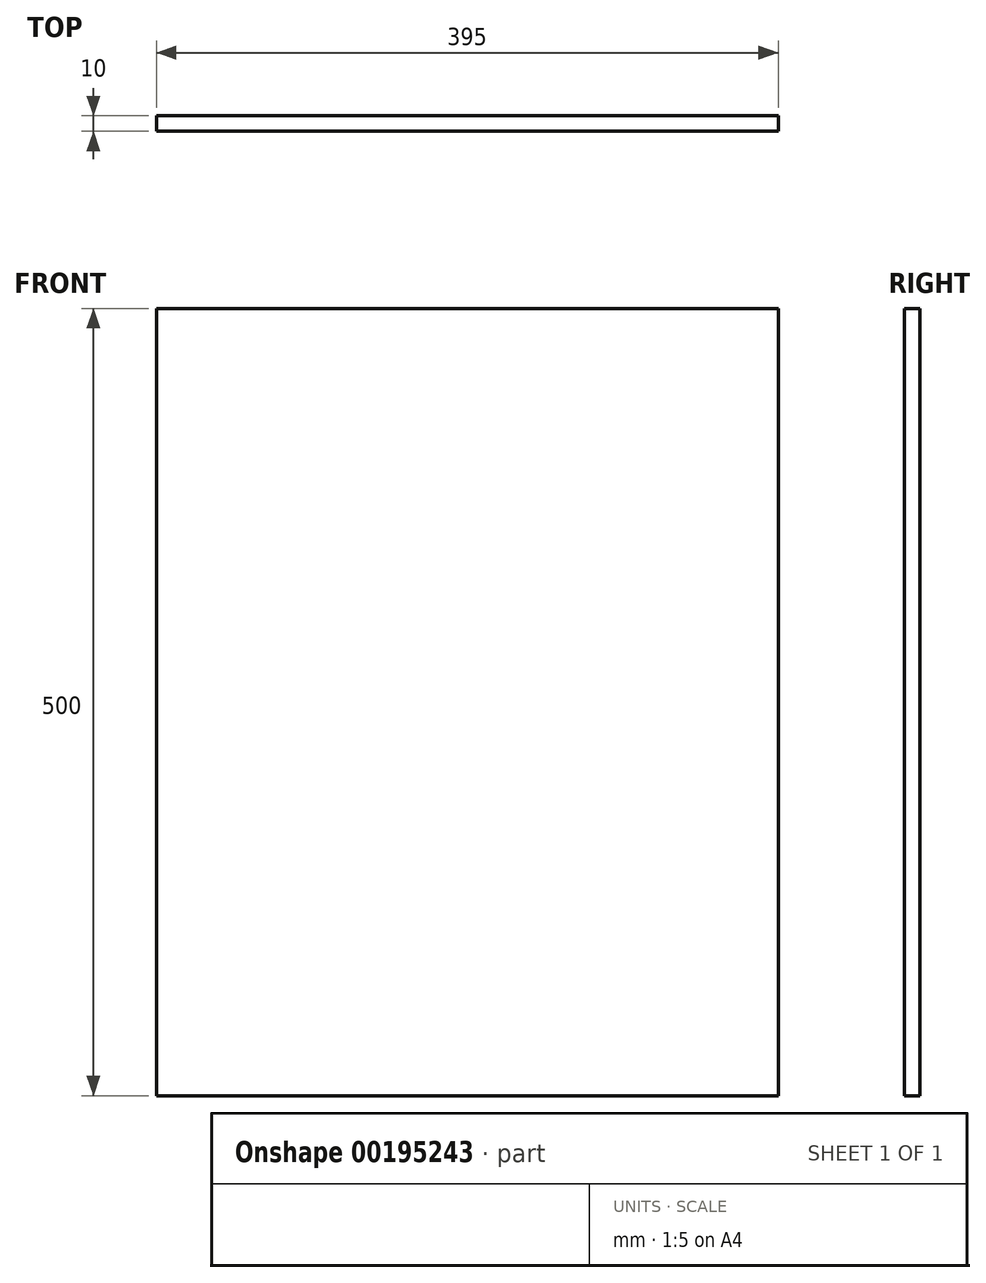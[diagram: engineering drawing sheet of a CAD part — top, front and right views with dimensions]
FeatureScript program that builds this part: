
annotation { "Feature Type Name" : "Feature", "Feature Type Description" : "" }
export const myFeature = defineFeature(function(context is Context, id is Id, definition is map)
    precondition{}
    {
        {
            var Q0;
            Q0=qCreatedBy(makeId("Front.planeOp"),FACE);
            var sketch = newSketch(context, id + "F1", { "sketchPlane" : qUnion([Q0])});
            skLineSegment(sketch, "E0.bottom", {"start": v(-197.5, 250) * mm, "end": v(197.5, 250) * mm});
            skLineSegment(sketch, "E0.top", {"start": v(-197.5, -250) * mm, "end": v(197.5, -250) * mm});
            skLineSegment(sketch, "E0.left", {"start": v(-197.5, 250) * mm, "end": v(-197.5, -250) * mm});
            skLineSegment(sketch, "E0.right", {"start": v(197.5, 250) * mm, "end": v(197.5, -250) * mm});
            skPoint(sketch, "E0.middle", {"position": v(0, 0) * mm});
            skSolve(sketch);
        }
        {
            var Q0;
            Q0=makeQuery(id+"F1.imprint","IMPRINT",FACE,{"disambiguationData":[TD([[makeQuery(id+"F1.imprint","IMPRINT",EDGE,{"derivedFrom":sQuery(id+"F1.wireOp",EDGE,"E0.bottom")}),-1.0]])]});
            extrude(context, id + "F0", {"entities" : qUnion([Q0]), "depth" : 10 * mm});
        }
    });
